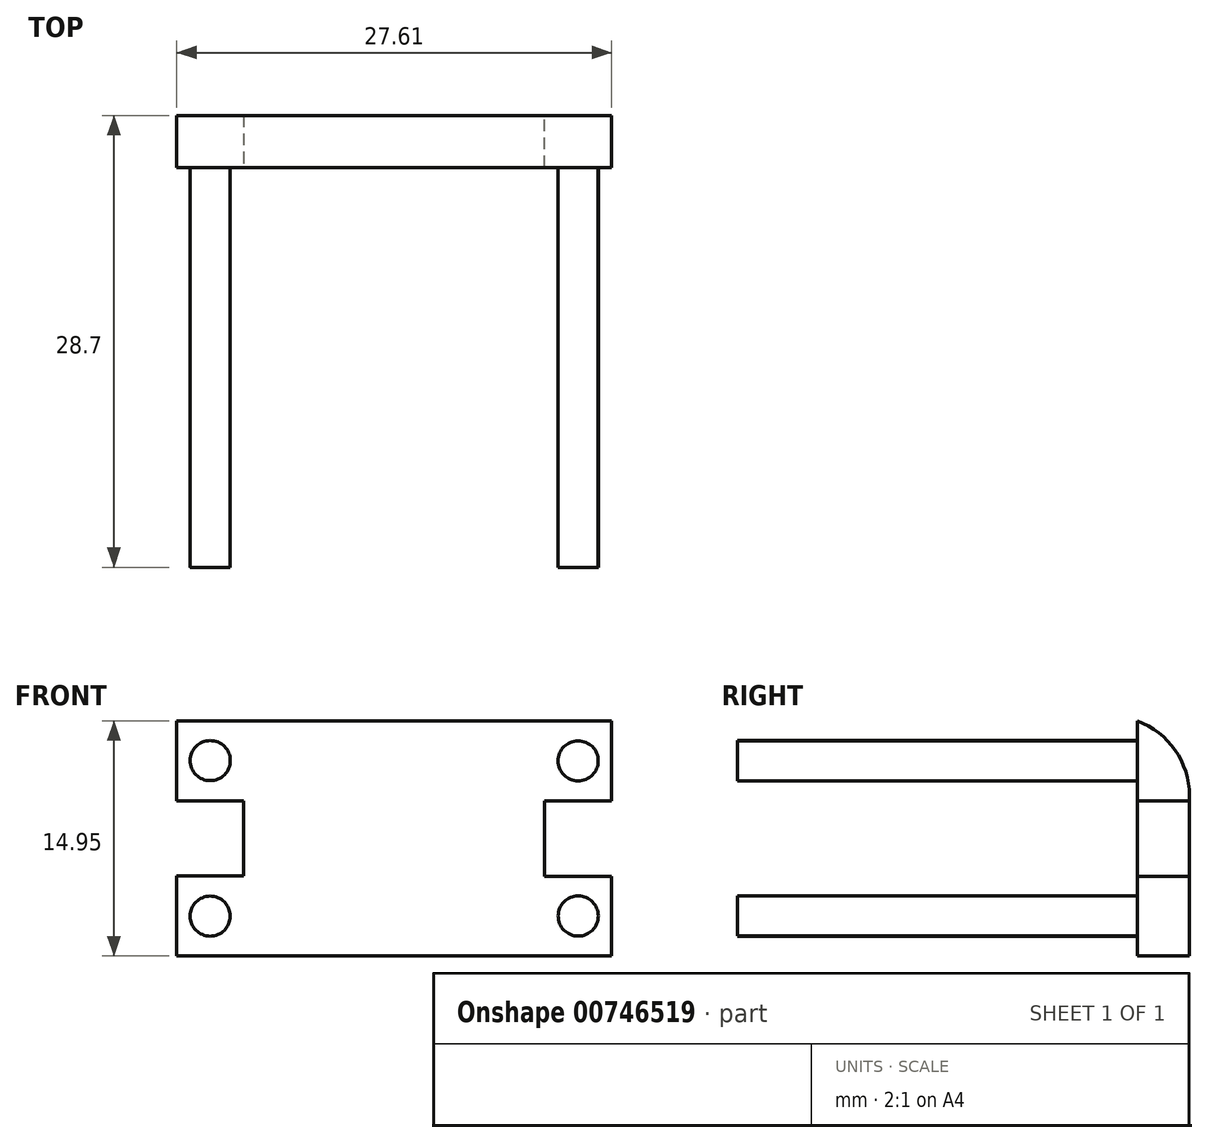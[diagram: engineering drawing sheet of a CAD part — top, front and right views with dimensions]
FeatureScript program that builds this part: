
annotation { "Feature Type Name" : "Feature", "Feature Type Description" : "" }
export const myFeature = defineFeature(function(context is Context, id is Id, definition is map)
    precondition{}
    {
        {
            var Q0;
            Q0=qCreatedBy(makeId("Front.planeOp"),FACE);
            var sketch = newSketch(context, id + "F0", { "sketchPlane" : qUnion([Q0])});
            skLineSegment(sketch, "E0.bottom", {"start": v(-8.97, 22.47) * mm, "end": v(10.16, 22.47) * mm});
            skLineSegment(sketch, "E0.top", {"start": v(-8.97, 7.52) * mm, "end": v(10.16, 7.52) * mm});
            skLineSegment(sketch, "E0.left", {"start": v(-8.97, 22.47) * mm, "end": v(-8.97, 7.52) * mm});
            skLineSegment(sketch, "E0.right", {"start": v(10.16, 22.47) * mm, "end": v(10.16, 7.52) * mm});
            skSolve(sketch);
        }
        {
            var Q0;
            Q0 = qSketchRegion(id + "F0", true);
            extrude(context, id + "F1", {"entities" : qUnion([Q0]), "depth" : 3.3 * mm, "offsetDistance" : 25.4 * mm});
        }
        {
            var Q0;
            Q0=makeQuery(id+"F1.opExtrude","SWEPT_FACE",FACE,{"disambiguationData":[OSD([sQuery(id+"F0.wireOp",EDGE,"E0.left")])]});
            var sketch = newSketch(context, id + "F2", { "sketchPlane" : qUnion([Q0])});
            skLineSegment(sketch, "E1.bottom", {"start": v(0, 22.47) * mm, "end": v(3.3, 22.47) * mm});
            skLineSegment(sketch, "E1.top", {"start": v(0, 17.39) * mm, "end": v(3.3, 17.39) * mm});
            skLineSegment(sketch, "E1.left", {"start": v(0, 22.47) * mm, "end": v(0, 17.39) * mm});
            skLineSegment(sketch, "E1.right", {"start": v(3.3, 22.47) * mm, "end": v(3.3, 17.39) * mm});
            skSolve(sketch);
        }
        {
            var Q0;
            {var subQ0=sQuery(id+"F2.wireOp",EDGE,"E1.top");Q0=makeQuery(id+"F2.imprint","IMPRINT",FACE,{"disambiguationData":[TD([[makeQuery(id+"F2.imprint","IMPRINT",EDGE,{"derivedFrom":subQ0}),-1.0]])]});}
            var sketch = newSketch(context, id + "F3", { "sketchPlane" : qUnion([Q0])});
            skLineSegment(sketch, "E2.bottom", {"start": v(0, 7.53) * mm, "end": v(3.3, 7.53) * mm});
            skLineSegment(sketch, "E2.top", {"start": v(0, 12.61) * mm, "end": v(3.3, 12.61) * mm});
            skLineSegment(sketch, "E2.left", {"start": v(0, 7.53) * mm, "end": v(0, 12.61) * mm});
            skLineSegment(sketch, "E2.right", {"start": v(3.3, 7.53) * mm, "end": v(3.3, 12.61) * mm});
            skSolve(sketch);
        }
        {
            var Q0;
            Q0=makeQuery(id+"F2.imprint","IMPRINT",FACE,{"disambiguationData":[TD([[makeQuery(id+"F2.imprint","IMPRINT",EDGE,{"derivedFrom":sQuery(id+"F2.wireOp",EDGE,"E1.bottom")}),1.0]])]});
            extrude(context, id + "F4", {"entities" : qUnion([Q0]), "operationType" : NewBodyOperationType.ADD, "depth" : 4.24 * mm, "offsetDistance" : 25.4 * mm});
        }
        {
            var Q0;
            Q0=makeQuery(id+"F3.imprint","IMPRINT",FACE,{"disambiguationData":[TD([[makeQuery(id+"F3.imprint","IMPRINT",EDGE,{"derivedFrom":sQuery(id+"F3.wireOp",EDGE,"E2.bottom")}),1.0]])]});
            extrude(context, id + "F5", {"entities" : qUnion([Q0]), "operationType" : NewBodyOperationType.ADD, "depth" : 4.24 * mm, "offsetDistance" : 25.4 * mm});
        }
        {
            var Q0;
            Q0=makeQuery(id+"F1.opExtrude","SWEPT_FACE",FACE,{"disambiguationData":[OSD([sQuery(id+"F0.wireOp",EDGE,"E0.right")])]});
            var sketch = newSketch(context, id + "F6", { "sketchPlane" : qUnion([Q0])});
            skLineSegment(sketch, "E3.bottom", {"start": v(-3.3, 22.47) * mm, "end": v(0, 22.47) * mm});
            skLineSegment(sketch, "E3.top", {"start": v(-3.3, 17.39) * mm, "end": v(0, 17.39) * mm});
            skLineSegment(sketch, "E3.left", {"start": v(-3.3, 22.47) * mm, "end": v(-3.3, 17.39) * mm});
            skLineSegment(sketch, "E3.right", {"start": v(0, 22.47) * mm, "end": v(0, 17.39) * mm});
            skLineSegment(sketch, "E4.bottom", {"start": v(-3.3, 7.52) * mm, "end": v(0, 7.52) * mm});
            skLineSegment(sketch, "E4.top", {"start": v(-3.3, 12.6) * mm, "end": v(0, 12.6) * mm});
            skLineSegment(sketch, "E4.left", {"start": v(-3.3, 7.52) * mm, "end": v(-3.3, 12.6) * mm});
            skLineSegment(sketch, "E4.right", {"start": v(0, 7.52) * mm, "end": v(0, 12.6) * mm});
            skSolve(sketch);
        }
        {
            var Q0;
            Q0=makeQuery(id+"F6.imprint","IMPRINT",FACE,{"disambiguationData":[TD([[makeQuery(id+"F6.imprint","IMPRINT",EDGE,{"derivedFrom":sQuery(id+"F6.wireOp",EDGE,"E3.bottom")}),-1.0]])]});
            var Q1;
            Q1=makeQuery(id+"F6.imprint","IMPRINT",FACE,{"disambiguationData":[TD([[makeQuery(id+"F6.imprint","IMPRINT",EDGE,{"derivedFrom":sQuery(id+"F6.wireOp",EDGE,"E4.bottom")}),1.0]])]});
            extrude(context, id + "F7", {"entities" : qUnion([Q0, Q1]), "operationType" : NewBodyOperationType.ADD, "depth" : 4.24 * mm, "offsetDistance" : 25.4 * mm});
        }
        {
            var Q0;
            Q0=makeQuery(id+"F7.boolean.opBoolean","MERGE",FACE,{"derivedFrom":[makeQuery(id+"F5.boolean.opBoolean","MERGE",FACE,{"derivedFrom":[makeQuery(id+"F4.boolean.opBoolean","MERGE",FACE,{"derivedFrom":[makeQuery(id+"F1.opExtrude","CAP_FACE",FACE,{"disambiguationData":[OSD([sQuery(id+"F0.wireOp",EDGE,"E0.bottom"),sQuery(id+"F0.wireOp",EDGE,"E0.top"),sQuery(id+"F0.wireOp",EDGE,"E0.left"),sQuery(id+"F0.wireOp",EDGE,"E0.right")])],"isStart":false}),makeQuery(id+"F4.opExtrude","SWEPT_FACE",FACE,{"disambiguationData":[OSD([sQuery(id+"F2.wireOp",EDGE,"E1.right")])]})]}),makeQuery(id+"F5.opExtrude","SWEPT_FACE",FACE,{"disambiguationData":[OSD([sQuery(id+"F3.wireOp",EDGE,"E2.right")])]})]}),makeQuery(id+"F7.opExtrude","SWEPT_FACE",FACE,{"disambiguationData":[OSD([sQuery(id+"F6.wireOp",EDGE,"E3.left")])]}),makeQuery(id+"F7.opExtrude","SWEPT_FACE",FACE,{"disambiguationData":[OSD([sQuery(id+"F6.wireOp",EDGE,"E4.left")])]})]});
            var sketch = newSketch(context, id + "F8", { "sketchPlane" : qUnion([Q0])});
            skLineSegment(sketch, "E5.bottom", {"start": v(-13.21, 22.47) * mm, "end": v(-8.97, 22.47) * mm});
            skLineSegment(sketch, "E5.top", {"start": v(-13.21, 17.39) * mm, "end": v(-8.97, 17.39) * mm});
            skLineSegment(sketch, "E5.left", {"start": v(-13.21, 22.47) * mm, "end": v(-13.21, 17.39) * mm});
            skLineSegment(sketch, "E5.right", {"start": v(-8.97, 22.47) * mm, "end": v(-8.97, 17.39) * mm});
            skLineSegment(sketch, "E6.bottom", {"start": v(-8.97, 12.61) * mm, "end": v(-13.21, 12.61) * mm});
            skLineSegment(sketch, "E6.top", {"start": v(-8.97, 7.53) * mm, "end": v(-13.21, 7.53) * mm});
            skLineSegment(sketch, "E6.left", {"start": v(-8.97, 12.61) * mm, "end": v(-8.97, 7.53) * mm});
            skLineSegment(sketch, "E6.right", {"start": v(-13.21, 12.61) * mm, "end": v(-13.21, 7.53) * mm});
            skLineSegment(sketch, "E7.bottom", {"start": v(10.16, 17.39) * mm, "end": v(14.4, 17.39) * mm});
            skLineSegment(sketch, "E7.top", {"start": v(10.16, 22.47) * mm, "end": v(14.4, 22.47) * mm});
            skLineSegment(sketch, "E7.left", {"start": v(10.16, 17.39) * mm, "end": v(10.16, 22.47) * mm});
            skLineSegment(sketch, "E7.right", {"start": v(14.4, 17.39) * mm, "end": v(14.4, 22.47) * mm});
            skLineSegment(sketch, "E8.bottom", {"start": v(10.16, 12.6) * mm, "end": v(14.4, 12.6) * mm});
            skLineSegment(sketch, "E8.top", {"start": v(10.16, 7.52) * mm, "end": v(14.4, 7.52) * mm});
            skLineSegment(sketch, "E8.left", {"start": v(10.16, 12.6) * mm, "end": v(10.16, 7.52) * mm});
            skLineSegment(sketch, "E8.right", {"start": v(14.4, 12.6) * mm, "end": v(14.4, 7.52) * mm});
            skLineSegment(sketch, "E9", {"start": v(10.16, 17.39) * mm, "end": v(10.16, 19.93) * mm});
            skLineSegment(sketch, "E10", {"start": v(10.16, 19.93) * mm, "end": v(12.28, 19.93) * mm});
            skPoint(sketch, "E10.endSnap0", {"position": v(12.28, 22.47) * mm});
            skLineSegment(sketch, "E11", {"start": v(12.28, 19.93) * mm, "end": v(12.28, 22.47) * mm});
            skLineSegment(sketch, "E12", {"start": v(10.16, 12.6) * mm, "end": v(12.28, 12.6) * mm});
            skLineSegment(sketch, "E13", {"start": v(12.28, 12.6) * mm, "end": v(12.28, 10.06) * mm});
            skPoint(sketch, "E13.endSnap0", {"position": v(10.16, 10.06) * mm});
            skLineSegment(sketch, "E14", {"start": v(12.28, 10.06) * mm, "end": v(10.16, 10.06) * mm});
            skLineSegment(sketch, "E15", {"start": v(-8.97, 22.47) * mm, "end": v(-11.1, 22.47) * mm});
            skLineSegment(sketch, "E16", {"start": v(-11.1, 22.47) * mm, "end": v(-11.1, 19.93) * mm});
            skLineSegment(sketch, "E17", {"start": v(-11.1, 19.93) * mm, "end": v(-8.97, 19.93) * mm});
            skLineSegment(sketch, "E18", {"start": v(-8.97, 12.61) * mm, "end": v(-11.1, 12.61) * mm});
            skLineSegment(sketch, "E19", {"start": v(-11.1, 12.61) * mm, "end": v(-11.1, 10.06) * mm});
            skLineSegment(sketch, "E20", {"start": v(-11.1, 10.06) * mm, "end": v(-8.97, 10.06) * mm});
            skSolve(sketch);
        }
        {
            var Q0;
            Q0=makeQuery(id+"F8.imprint","IMPRINT",FACE,{"disambiguationData":[TD([[makeQuery(id+"F8.imprint","IMPRINT",EDGE,{"derivedFrom":sQuery(id+"F8.wireOp",EDGE,"E5.bottom")}),-1.0]])]});
            var sketch = newSketch(context, id + "F9", { "sketchPlane" : qUnion([Q0])});
            skCircle(sketch, "E21", {"center": v(-11.09, 19.94) * mm, "radius": 1.27 * mm});
            skCircle(sketch, "E22", {"center": v(-11.1, 10.06) * mm, "radius": 1.27 * mm});
            skCircle(sketch, "E23", {"center": v(12.28, 19.92) * mm, "radius": 1.27 * mm});
            skCircle(sketch, "E24", {"center": v(12.28, 10.07) * mm, "radius": 1.27 * mm});
            skSolve(sketch);
        }
        {
            var Q0;
            Q0 = qSketchRegion(id + "F9", true);
            extrude(context, id + "F10", {"entities" : qUnion([Q0]), "operationType" : NewBodyOperationType.ADD, "depth" : 25.4 * mm, "offsetDistance" : 25.4 * mm});
        }
        {
            var Q0;
            Q0=makeQuery(id+"F7.boolean.opBoolean","MERGE",EDGE,{"derivedFrom":[makeQuery(id+"F4.boolean.opBoolean","MERGE",EDGE,{"derivedFrom":[makeQuery(id+"F1.opExtrude","CAP_EDGE",EDGE,{"disambiguationData":[OSD([sQuery(id+"F0.wireOp",EDGE,"E0.bottom")])],"isStart":true}),makeQuery(id+"F4.opExtrude","SWEPT_EDGE",EDGE,{"disambiguationData":[OSD([sQuery(id+"F2.wireOp",EDGE,"E1.bottom"),sQuery(id+"F2.wireOp",EDGE,"E1.left")])]})]}),makeQuery(id+"F7.opExtrude","SWEPT_EDGE",EDGE,{"disambiguationData":[OSD([sQuery(id+"F6.wireOp",EDGE,"E3.bottom"),sQuery(id+"F6.wireOp",EDGE,"E3.right")])]})]});
            fillet(context, id + "F11", {"entities" : qUnion([Q0]), "radius" : 5.08 * mm, "tangentPropagation" : true, "allowEdgeOverflow" : false});
        }
    });
